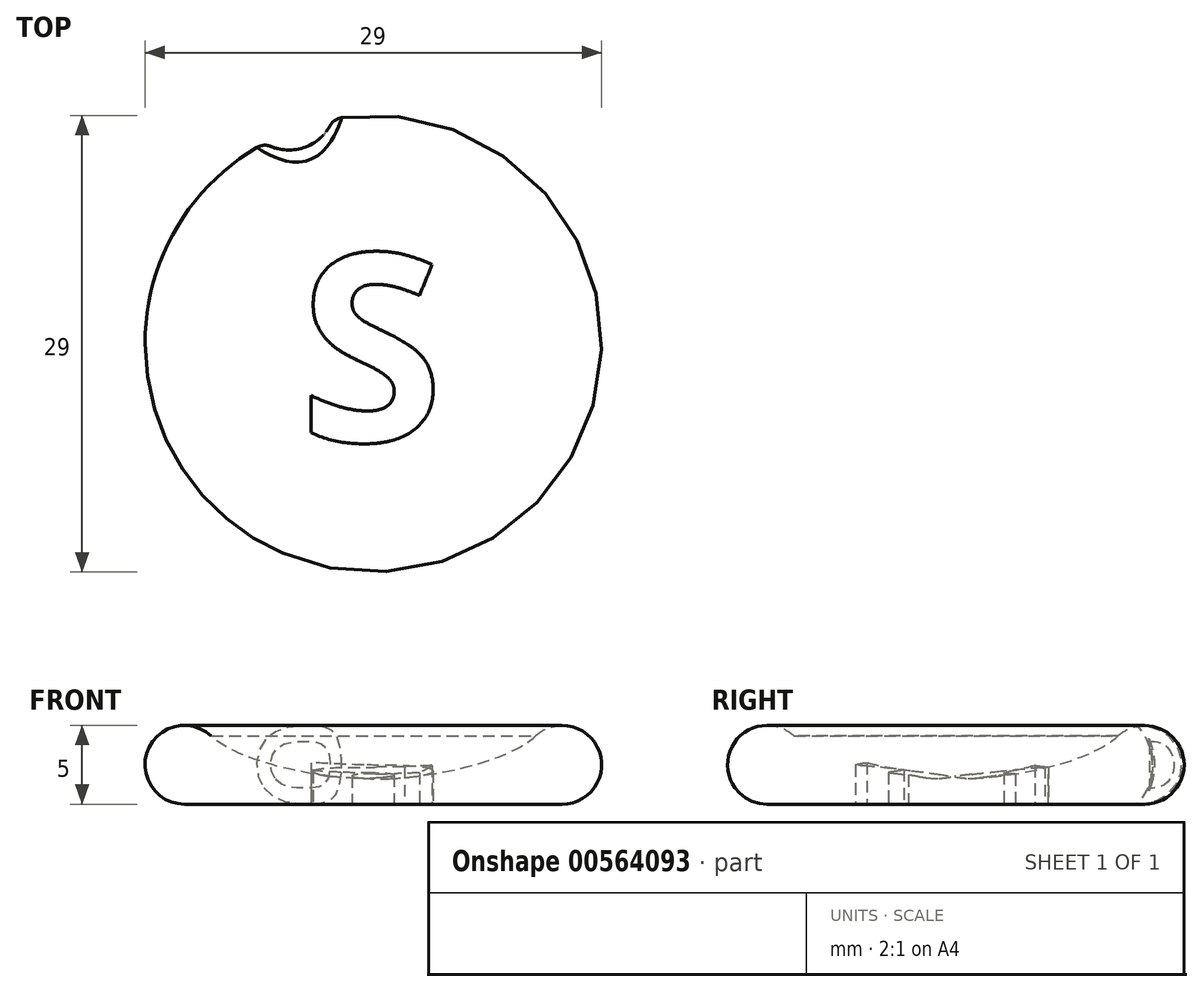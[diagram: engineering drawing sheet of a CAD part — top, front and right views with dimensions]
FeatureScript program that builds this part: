
annotation { "Feature Type Name" : "Feature", "Feature Type Description" : "" }
export const myFeature = defineFeature(function(context is Context, id is Id, definition is map)
    precondition{}
    {
        {
            var Q0;
            Q0=qCreatedBy(makeId("Front.planeOp"),FACE);
            var sketch = newSketch(context, id + "F0", { "sketchPlane" : qUnion([Q0])});
            skCircle(sketch, "E0", {"center": v(-12, 2.5) * mm, "radius": 2.5 * mm});
            skLineSegment(sketch, "E1", {"start": v(0, 0) * mm, "end": v(0, 1.58) * mm});
            skFitSpline(sketch, "E2", {"points": [v(0, 1.58) * mm, v(-10.3, 4.33) * mm], "startDerivative": vector(-8.66, -0.04) * mm, "endDerivative": vector(-5.93, 5.53) * mm});
            skLineSegment(sketch, "E3", {"start": v(0, 0) * mm, "end": v(-12, 0) * mm});
            skSolve(sketch);
        }
        {
            var Q0;
            {var subQ0=sQuery(id+"F0.wireOp",EDGE,"E0");var subQ1=makeQuery(id+"F0.imprint","INTERSECT",VERTEX,{"derivedFrom":[subQ0,sQuery(id+"F0.wireOp",EDGE,"E2")]});Q0=makeQuery(id+"F0.imprint","IMPRINT",FACE,{"disambiguationData":[TD([[makeQuery(id+"F0.imprint","IMPRINT",EDGE,{"disambiguationData":[TD([[subQ1,-1.0]])],"derivedFrom":subQ0}),1.0]])]});}
            var Q1;
            Q1=makeQuery(id+"F0.imprint","IMPRINT",FACE,{"disambiguationData":[TD([[makeQuery(id+"F0.imprint","IMPRINT",EDGE,{"derivedFrom":sQuery(id+"F0.wireOp",EDGE,"E1")}),1.0]])]});
            var Q2;
            Q2=sQuery(id+"F0.wireOp",EDGE,"E1");
            revolve(context, id + "F1", {"entities" : qUnion([Q0, Q1]), "axis" : qUnion([Q2]), "revolveType" : RevolveType.FULL});
        }
        {
            var Q0;
            Q0=qCreatedBy(makeId("Top.planeOp"),FACE);
            var sketch = newSketch(context, id + "F2", { "sketchPlane" : qUnion([Q0])});
            skCircle(sketch, "E4", {"center": v(-5.36, 15.3) * mm, "radius": 3 * mm});
            skSolve(sketch);
        }
        {
            var Q0;
            Q0=makeQuery(id+"F2.imprint","IMPRINT",FACE,{"disambiguationData":[TD([[makeQuery(id+"F2.imprint","IMPRINT",EDGE,{"derivedFrom":sQuery(id+"F2.wireOp",EDGE,"E4")}),1.0]])]});
            var Q1;
            Q1=sQuery(id+"F2.wireOp",EDGE,"E4");
            extrude(context, id + "F3", {"entities" : qUnion([Q0]), "operationType" : NewBodyOperationType.REMOVE, "surfaceEntities" : qUnion([Q1]), "depth" : 10 * mm, "offsetDistance" : 25 * mm});
        }
        {
            var Q0;
            Q0=makeQuery(id+"F3.boolean.opBoolean","COPY",FACE,{"derivedFrom":makeQuery(id+"F3.opExtrude","SWEPT_FACE",FACE,{"disambiguationData":[OSD([sQuery(id+"F2.wireOp",EDGE,"E4")])]})});
            fillet(context, id + "F4", {"entities" : qUnion([Q0]), "radius" : 1 * mm, "tangentPropagation" : true, "allowEdgeOverflow" : false});
        }
        {
            var Q0;
            Q0=qCreatedBy(makeId("Top.planeOp"),FACE);
            var sketch = newSketch(context, id + "F5", { "sketchPlane" : qUnion([Q0])});
            skText(sketch, "E5", { "text": "S", "fontName": "OpenSans-Bold.ttf"});
            const initialGuessF5  = {"E5": [-0.00472, -0.0062, 1, 0, 0.012]};
            skSetInitialGuess(sketch, initialGuessF5);
            skSolve(sketch);
        }
        {
            var Q0;
            Q0 = qSketchRegion(id + "F5", true);
            extrude(context, id + "F6", {"entities" : qUnion([Q0]), "operationType" : NewBodyOperationType.REMOVE, "depth" : 25 * mm, "offsetDistance" : 25 * mm});
        }
    });
